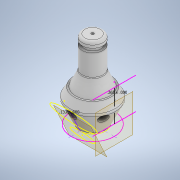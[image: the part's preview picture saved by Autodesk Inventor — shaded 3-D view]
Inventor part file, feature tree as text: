
AUTODESK INVENTOR PART (.ipt)
format: ipt  version: 2020 (Build 240168000, 168)  size: 323,584 bytes
history: native  units: in
note: dims shown in document units (in); Inventor stores cm internally (conversion verified against a paired STEP export)
features: sketch x6, hole x4, plane x2, fillet x2, revolve x1, pattern_circular x1
ambient origin geometry x8: Origin, YZ Plane, XZ Plane, XY Plane, X Axis, Y Axis, Z Axis, Center Point
bodies: Solid1 (feature_tree)
feature tree (16):
  revolve  "Revolution1"  [1 undecoded]
  hole  "Hole4"  [1 undecoded]
  hole  "Hole8"  [1 undecoded]
  sketch  "Sketch13"  dims[d2=90.0deg d3=0.057in]
  plane  "Work Plane6"
  sketch  "Sketch14"  dims[d4=0.095in d5=0.125in]
  sketch  "Sketch29"  dims[d24=0.4466in d25=0.125in]
  plane  "Work Plane5"
  sketch  "Sketch30"  dims[d54=0.3779in d72=0.3779in d83=0.75in d84=0.75in d85=0.0625in d86=0.75in d87=0.375in d88=0.25in d89=0.5635in d90=1.1in d91=0.8108in d92=0.2645in d121=0.196in d122=0.25in d123=0.375in d124=0.25in d125=0.5635in d126=0.25in d127=0.0in d137=0.3779in d155=0.3779in d173=0.3779in d191=0.3779in d221=0.3779in d239=0.3779in d253=0.4466in d254=0.1325in d255=0.0625in d256=0.25in d257=0.375in d258=0.25in d259=0.5635in d260=0.55in d261=0.0in d262=0.213in d263=0.25in d264=0.375in d265=0.25in d266=0.5635in d267=0.25in d268=0.0in d269=1.5748in d270=1.3743in d272=0.0625in d273=0.0625in]
  hole  "Hole9"  [1 undecoded]
  hole  "Hole10"  [1 undecoded]
  pattern_circular  "Circular Pattern7"  [2 undecoded]
  fillet  "Fillet1"  Radius=0.75in
  fillet  "Fillet2"  Radius=0.75in
  sketch  "Sketch12"  dims[d0=0.239in d1=0.5in]
  sketch  "Sketch16"  dims[d6=90.0deg d23=0.65in]
note: 7 required parameter values undecoded (feature->parameter linkage not recoverable at this tier; creation-order binding heuristic only, values carry confidence <= 0.55)